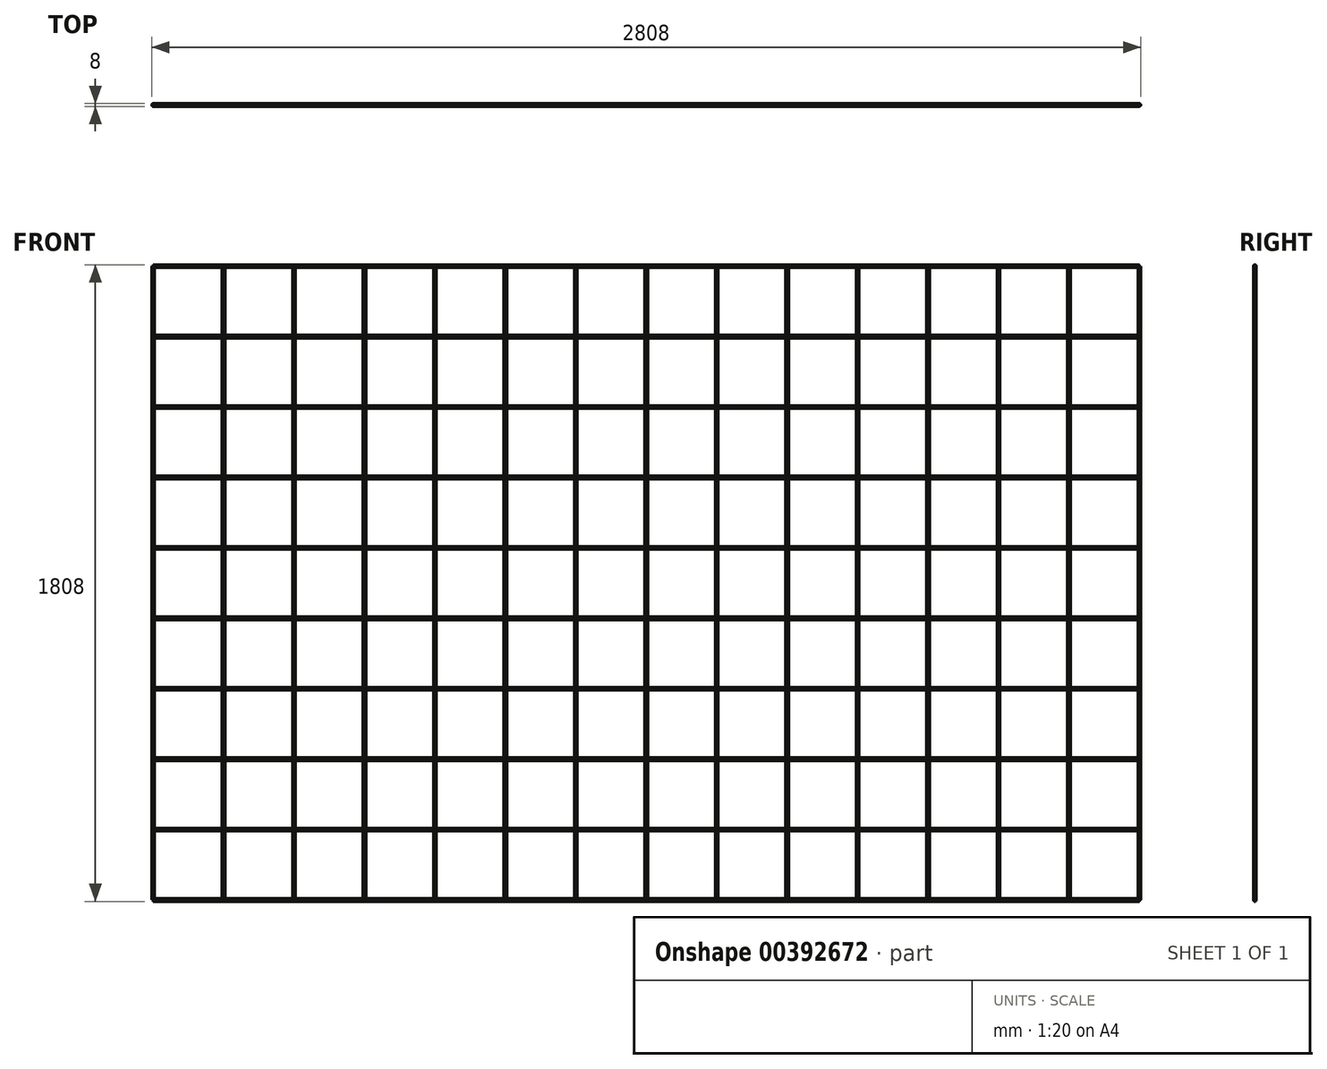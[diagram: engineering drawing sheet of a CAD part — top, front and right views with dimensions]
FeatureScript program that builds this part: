
annotation { "Feature Type Name" : "Feature", "Feature Type Description" : "" }
export const myFeature = defineFeature(function(context is Context, id is Id, definition is map)
    precondition{}
    {
        {
            var Q0;
            Q0=qCreatedBy(makeId("Right.planeOp"),FACE);
            var sketch = newSketch(context, id + "F0", { "sketchPlane" : qUnion([Q0])});
            skLineSegment(sketch, "E0", {"start": v(0, 0) * mm, "end": v(0, -1800) * mm});
            skLineSegment(sketch, "E1", {"start": v(0, 0) * mm, "end": v(0, -200) * mm});
            skLineSegment(sketch, "E2", {"start": v(0, -200) * mm, "end": v(0, -400) * mm});
            skLineSegment(sketch, "E3", {"start": v(0, -400) * mm, "end": v(0, -600) * mm});
            skLineSegment(sketch, "E4", {"start": v(0, -600) * mm, "end": v(0, -800) * mm});
            skLineSegment(sketch, "E5", {"start": v(0, -800) * mm, "end": v(0, -1000) * mm});
            skLineSegment(sketch, "E6", {"start": v(0, -1000) * mm, "end": v(0, -1200) * mm});
            skLineSegment(sketch, "E7", {"start": v(0, -1200) * mm, "end": v(0, -1400) * mm});
            skLineSegment(sketch, "E8", {"start": v(0, -1400) * mm, "end": v(0, -1600) * mm});
            skLineSegment(sketch, "E9", {"start": v(0, -1600) * mm, "end": v(0, -1800) * mm});
            skCircle(sketch, "E10", {"center": v(0, 0) * mm, "radius": 4 * mm});
            skCircle(sketch, "E11", {"center": v(0, -200) * mm, "radius": 4 * mm});
            skCircle(sketch, "E12", {"center": v(0, -400) * mm, "radius": 4 * mm});
            skCircle(sketch, "E13", {"center": v(0, -600) * mm, "radius": 4 * mm});
            skCircle(sketch, "E14", {"center": v(0, -800) * mm, "radius": 4 * mm});
            skCircle(sketch, "E15", {"center": v(0, -1000) * mm, "radius": 4 * mm});
            skCircle(sketch, "E16", {"center": v(0, -1200) * mm, "radius": 4 * mm});
            skCircle(sketch, "E17", {"center": v(0, -1400) * mm, "radius": 4 * mm});
            skCircle(sketch, "E18", {"center": v(0, -1600) * mm, "radius": 4 * mm});
            skCircle(sketch, "E19", {"center": v(0, -1800) * mm, "radius": 4 * mm});
            skSolve(sketch);
        }
        {
            var Q0;
            Q0 = qSketchRegion(id + "F0", true);
            extrude(context, id + "F1", {"entities" : qUnion([Q0]), "depth" : 2800 * mm});
        }
        {
            var Q0;
            Q0=qCreatedBy(makeId("Top.planeOp"),FACE);
            var sketch = newSketch(context, id + "F2", { "sketchPlane" : qUnion([Q0])});
            skLineSegment(sketch, "E20", {"start": v(0, 0) * mm, "end": v(200, 0) * mm});
            skLineSegment(sketch, "E21", {"start": v(200, 0) * mm, "end": v(400, 0) * mm});
            skLineSegment(sketch, "E22", {"start": v(400, 0) * mm, "end": v(600, 0) * mm});
            skPoint(sketch, "E22.endSnap0", {"position": v(300, 0) * mm});
            skLineSegment(sketch, "E23", {"start": v(600, 0) * mm, "end": v(800, 0) * mm});
            skLineSegment(sketch, "E24", {"start": v(800, 0) * mm, "end": v(1000, 0) * mm});
            skLineSegment(sketch, "E25", {"start": v(1000, 0) * mm, "end": v(1200, 0) * mm});
            skLineSegment(sketch, "E26", {"start": v(1200, 0) * mm, "end": v(1400, 0) * mm});
            skLineSegment(sketch, "E27", {"start": v(1400, 0) * mm, "end": v(1600, 0) * mm});
            skLineSegment(sketch, "E28", {"start": v(1600, 0) * mm, "end": v(1800, 0) * mm});
            skLineSegment(sketch, "E29", {"start": v(1800, 0) * mm, "end": v(2000, 0) * mm});
            skPoint(sketch, "E29.endSnap0", {"position": v(1700, 0) * mm});
            skLineSegment(sketch, "E30", {"start": v(2000, 0) * mm, "end": v(2200, 0) * mm});
            skPoint(sketch, "E30.endSnap0", {"position": v(1900, 0) * mm});
            skLineSegment(sketch, "E31", {"start": v(2200, 0) * mm, "end": v(2400, 0) * mm});
            skLineSegment(sketch, "E32", {"start": v(2400, 0) * mm, "end": v(2600, 0) * mm});
            skLineSegment(sketch, "E33", {"start": v(2600, 0) * mm, "end": v(2800, 0) * mm});
            skCircle(sketch, "E34", {"center": v(2800, 0) * mm, "radius": 4 * mm});
            skCircle(sketch, "E35", {"center": v(2600, 0) * mm, "radius": 4 * mm});
            skCircle(sketch, "E36", {"center": v(2400, 0) * mm, "radius": 4 * mm});
            skCircle(sketch, "E37", {"center": v(2200, 0) * mm, "radius": 4 * mm});
            skCircle(sketch, "E38", {"center": v(2000, 0) * mm, "radius": 4 * mm});
            skCircle(sketch, "E39", {"center": v(1800, 0) * mm, "radius": 4 * mm});
            skCircle(sketch, "E40", {"center": v(1200, 0) * mm, "radius": 4 * mm});
            skCircle(sketch, "E41", {"center": v(1000, 0) * mm, "radius": 4 * mm});
            skCircle(sketch, "E42", {"center": v(800, 0) * mm, "radius": 4 * mm});
            skCircle(sketch, "E43", {"center": v(600, 0) * mm, "radius": 4 * mm});
            skCircle(sketch, "E44", {"center": v(400, 0) * mm, "radius": 4 * mm});
            skCircle(sketch, "E45", {"center": v(1600, 0) * mm, "radius": 4 * mm});
            skCircle(sketch, "E46", {"center": v(1400, 0) * mm, "radius": 4 * mm});
            skCircle(sketch, "E47", {"center": v(200, 0) * mm, "radius": 4 * mm});
            skCircle(sketch, "E48", {"center": v(0, 0) * mm, "radius": 4 * mm});
            skSolve(sketch);
        }
        {
            var Q0;
            Q0 = qSketchRegion(id + "F2", true);
            extrude(context, id + "F3", {"entities" : qUnion([Q0]), "operationType" : NewBodyOperationType.ADD, "oppositeDirection" : true, "depth" : 1800 * mm});
        }
    });
